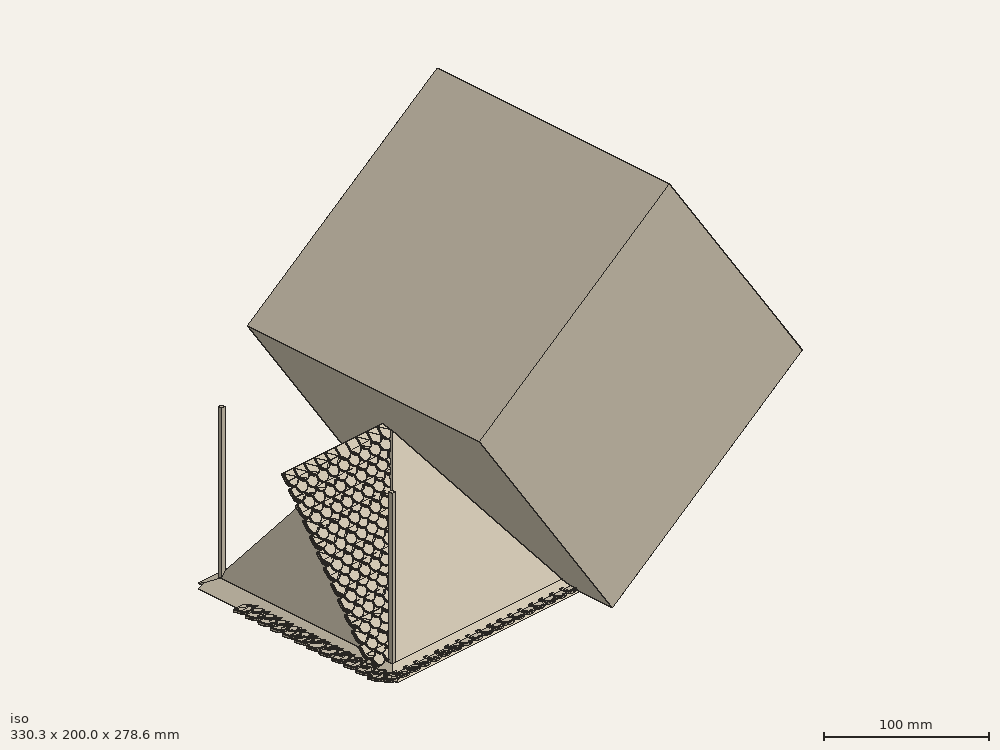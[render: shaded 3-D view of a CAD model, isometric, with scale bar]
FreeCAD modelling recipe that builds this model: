
FCSTD DOCUMENT  (FreeCAD 0.15R4671 (Git))
Label: tejado
License: All rights reserved
LicenseURL: http://en.wikipedia.org/wiki/All_rights_reserved
objects: Part::Box×20, Part::Cut×16, Part::FeaturePython×12, Sketcher::SketchObject×6, PartDesign::Pad×6, Part::Fillet×6, Part::Thickness×2, Part::MultiFuse×1
note: 75 computed .brp shape members not serialized (recipe doc carries the construction recipe); baked Part::Feature solids carry a one-line shape summary decoded from their .brp

FEATURE [Part::Box] Box  label="Cube"
  Height = 120
  Length = 144
  Width = 144
FEATURE [Part::Box] Box001  label="Cube001"
  Height = 70
  Length = 144
  Placement = pos=(0,0,0) rot=(0,-1,0;0.959931rad)
  Width = 144
FEATURE [Part::Box] Box002  label="Cube002"
  Height = 70
  Length = 144
  Placement = pos=(0,0,0) rot=(1,0,0;0.959931rad)
  Width = 144
FEATURE [Part::Box] Box003  label="Cube003"
  Height = 70
  Length = 144
  Placement = pos=(61.405,0,117.958) rot=(0,1,0;0.959931rad)
  Width = 144
FEATURE [Part::Box] Box004  label="Cube004"
  Height = 70
  Length = 144
  Placement = pos=(0,61.405,117.958) rot=(-1,0,0;0.959931rad)
  Width = 144
FEATURE [Part::Cut] Cut
  Base = -> Box
  Tool = -> Box001
FEATURE [Part::Cut] Cut001
  Base = -> Cut
  Tool = -> Box002
FEATURE [Part::Cut] Cut002
  Base = -> Cut001
  Tool = -> Box003
FEATURE [Part::Cut] Cut003  label="tejado_principal"
  Base = -> Cut002
  Tool = -> Box004
FEATURE [Part::Thickness] Thickness  label="tejado_principal_vaciado"
  Faces = -> Cut003 [Face1]
  Intersection = false
  Join = 0
  Mode = 0
  Placement = pos=(14,14,6.4) rot=(0,0,1;0rad)
  SelfIntersection = false
  Value = -2
FEATURE [Part::Box] Box005  label="Cube005"
  Height = 70
  Length = 172
  Width = 172
FEATURE [Part::Box] Box006  label="Cube006"
  Height = 70
  Length = 172
  Placement = pos=(0,0,0) rot=(1,0,0;0.436332rad)
  Width = 172
FEATURE [Part::Box] Box007  label="Cube007"
  Height = 70
  Length = 172
  Placement = pos=(0,0,0) rot=(0,-1,0;0.436332rad)
  Width = 172
FEATURE [Part::Box] Box008  label="Cube008"
  Height = 70
  Length = 172
  Placement = pos=(0,16.1151,72.6903) rot=(-1,0,0;0.436332rad)
  Width = 172
FEATURE [Part::Box] Box009  label="Cube009"
  Height = 70
  Length = 172
  Placement = pos=(16.1151,0,72.6903) rot=(0,1,0;0.436332rad)
  Width = 172
FEATURE [Part::Cut] Cut004
  Base = -> Box005
  Tool = -> Box006
FEATURE [Part::Cut] Cut005
  Base = -> Cut004
  Tool = -> Box007
FEATURE [Part::Cut] Cut006
  Base = -> Cut005
  Tool = -> Box008
FEATURE [Part::Cut] Cut007  label="faldones"
  Base = -> Cut006
  Tool = -> Box009
FEATURE [Part::Thickness] Thickness001  label="faldones_vaciado"
  Faces = -> Cut007 [Face1]
  Intersection = false
  Join = 0
  Mode = 0
  SelfIntersection = false
  Value = -2
FEATURE [Part::Box] Box010  label="Cube010"
  Height = 100
  Length = 172
  Placement = pos=(0,0,6.4) rot=(0,0,1;0rad)
  Width = 172
FEATURE [Part::Cut] Cut008  label="faldones_vaciado_completo"
  Base = -> Thickness001
  Tool = -> Box010
FEATURE [Part::Box] Box011  label="Cube011"
  Height = 10
  Length = 5
  Placement = pos=(0,0,-3) rot=(0,0,1;0rad)
  Width = 5
FEATURE [Part::Box] Box012  label="Cube012"
  Height = 10
  Length = 5
  Placement = pos=(0,167,-3) rot=(0,0,1;0rad)
  Width = 5
FEATURE [Part::Cut] Cut009
  Base = -> Cut008
  Tool = -> Box011
FEATURE [Part::Cut] Cut010  label="faldones_con_muescas"
  Base = -> Cut009
  Tool = -> Box012
FEATURE [Sketcher::SketchObject] Sketch
  Placement = pos=(9,10.5,0) rot=(0,0,1;3.14159rad)
  sketch-geometry (4):
    g0: LineSegment StartX=0 StartY=0 StartZ=0 EndX=4.1e-11 EndY=6 EndZ=0
    g1: LineSegment StartX=0 StartY=0 StartZ=0 EndX=9 EndY=0 EndZ=0
    g2: LineSegment StartX=9 StartY=0 StartZ=0 EndX=9 EndY=6 EndZ=0
    g3: ArcOfCircle CenterX=4.5 CenterY=5.99998 CenterZ=0 NormalX=0 NormalY=0 NormalZ=1 Radius=4.5 StartAngle=4.27504e-06 EndAngle=3.14159
  constraints (12):
    c: Coincident(g0,g-1)
    c: PointOnObject(g0,g-2)
    c: Coincident(g1,g-1)
    c: Horizontal(g1)
    c: Vertical(g2)
    c: Equal(g2,g0)
    c: Coincident(g3,g0)
    c: Coincident(g3,g2)
    c: DistanceX(g1) = 9
    c: Coincident(g1,g2)
    c: DistanceY(g0) = 6
    c: Radius(g3) = 4.5
FEATURE [PartDesign::Pad] Pad  label="teja"
  Length = 2
  Length2 = 100
  Placement = pos=(9,10.5,0) rot=(0,0,1;3.14159rad)
  Sketch = -> Sketch
  Type = 0
FEATURE [Part::Fillet] Fillet  label="teja_con_fillet"
  Base = -> Pad
  Edges = 4 edges r=0.5: [Edge4,Edge7,Edge10,Edge12]
FEATURE [Part::FeaturePython] Array  label="fila_tejas_par"  # Draft array (typed FeaturePython)
  Angle = 360
  ArrayType = 0
  Axis = (1,0,0)
  Base = -> Fillet
  Center = (0,0,0)
  Fuse = false
  IntervalAxis = (0,0,0)
  IntervalX = (9,0,0)
  IntervalY = (0,1,0)
  IntervalZ = (0,0,0)
  NumberPolar = 1
  NumberX = 20
  NumberY = 1
  NumberZ = 1
  Placement = pos=(0,0.102185,1.46132) rot=(-1,0,0;0.139626rad)
FEATURE [Sketcher::SketchObject] Sketch001
  Placement = pos=(9,10.5,0) rot=(0,0,1;3.14159rad)
  sketch-geometry (4):
    g0: LineSegment StartX=0 StartY=0 StartZ=0 EndX=4.1e-11 EndY=6 EndZ=0
    g1: LineSegment StartX=0 StartY=0 StartZ=0 EndX=9 EndY=0 EndZ=0
    g2: LineSegment StartX=9 StartY=0 StartZ=0 EndX=9 EndY=6 EndZ=0
    g3: ArcOfCircle CenterX=4.5 CenterY=5.99998 CenterZ=0 NormalX=0 NormalY=0 NormalZ=1 Radius=4.5 StartAngle=4.27504e-06 EndAngle=3.14159
  constraints (12):
    c: Coincident(g0,g-1)
    c: PointOnObject(g0,g-2)
    c: Coincident(g1,g-1)
    c: Horizontal(g1)
    c: Vertical(g2)
    c: Equal(g2,g0)
    c: Coincident(g3,g0)
    c: Coincident(g3,g2)
    c: DistanceX(g1) = 9
    c: Coincident(g1,g2)
    c: DistanceY(g0) = 6
    c: Radius(g3) = 4.5
FEATURE [PartDesign::Pad] Pad001  label="teja001"
  Length = 2
  Length2 = 100
  Placement = pos=(9,10.5,0) rot=(0,0,1;3.14159rad)
  Sketch = -> Sketch001
  Type = 0
FEATURE [Part::Fillet] Fillet001  label="teja_con_fillet001"
  Base = -> Pad001
  Edges = 4 edges r=0.5: [Edge4,Edge7,Edge10,Edge12]
FEATURE [Part::FeaturePython] Array001  label="fila_tejas_impar"  # Draft array (typed FeaturePython)
  Angle = 360
  ArrayType = 0
  Axis = (1,0,0)
  Base = -> Fillet001
  Center = (0,0,0)
  Fuse = false
  IntervalAxis = (0,0,0)
  IntervalX = (9,0,0)
  IntervalY = (0,1,0)
  IntervalZ = (0,0,0)
  NumberPolar = 1
  NumberX = 20
  NumberY = 1
  NumberZ = 1
  Placement = pos=(-4.5,6.10219,1.46132) rot=(-1,0,0;0.139626rad)
FEATURE [Part::FeaturePython] Array002  label="tejas"  # Draft array (typed FeaturePython)
  Angle = 360
  ArrayType = 0
  Axis = (0,0,1)
  Center = (0,0,0)
  Fuse = false
  IntervalAxis = (0,0,0)
  IntervalX = (1,0,0)
  IntervalY = (0,10.5,0)
  IntervalZ = (0,0,0)
  NumberPolar = 1
  NumberX = 1
  NumberY = 12
  NumberZ = 1
FEATURE [Sketcher::SketchObject] Sketch002
  Placement = pos=(9,10.5,0) rot=(0,0,1;3.14159rad)
  sketch-geometry (4):
    g0: LineSegment StartX=0 StartY=0 StartZ=0 EndX=4.1e-11 EndY=6 EndZ=0
    g1: LineSegment StartX=0 StartY=0 StartZ=0 EndX=9 EndY=0 EndZ=0
    g2: LineSegment StartX=9 StartY=0 StartZ=0 EndX=9 EndY=6 EndZ=0
    g3: ArcOfCircle CenterX=4.5 CenterY=5.99998 CenterZ=0 NormalX=0 NormalY=0 NormalZ=1 Radius=4.5 StartAngle=4.27504e-06 EndAngle=3.14159
  constraints (12):
    c: Coincident(g0,g-1)
    c: PointOnObject(g0,g-2)
    c: Coincident(g1,g-1)
    c: Horizontal(g1)
    c: Vertical(g2)
    c: Equal(g2,g0)
    c: Coincident(g3,g0)
    c: Coincident(g3,g2)
    c: DistanceX(g1) = 9
    c: Coincident(g1,g2)
    c: DistanceY(g0) = 6
    c: Radius(g3) = 4.5
FEATURE [PartDesign::Pad] Pad002  label="teja002"
  Length = 2
  Length2 = 100
  Placement = pos=(9,10.5,0) rot=(0,0,1;3.14159rad)
  Sketch = -> Sketch002
  Type = 0
FEATURE [Part::Fillet] Fillet002  label="teja_con_fillet002"
  Base = -> Pad002
  Edges = 4 edges r=0.5: [Edge4,Edge7,Edge10,Edge12]
FEATURE [Part::FeaturePython] Array003  label="fila_tejas_003"  # Draft array (typed FeaturePython)
  Angle = 360
  ArrayType = 0
  Axis = (1,0,0)
  Base = -> Fillet002
  Center = (0,0,0)
  Fuse = false
  IntervalAxis = (0,0,0)
  IntervalX = (9,0,0)
  IntervalY = (0,1,0)
  IntervalZ = (0,0,0)
  NumberPolar = 1
  NumberX = 20
  NumberY = 1
  NumberZ = 1
  Placement = pos=(0,0.102185,1.46132) rot=(-1,0,0;0.139626rad)
FEATURE [Sketcher::SketchObject] Sketch003
  Placement = pos=(9,10.5,0) rot=(0,0,1;3.14159rad)
  sketch-geometry (4):
    g0: LineSegment StartX=0 StartY=0 StartZ=0 EndX=4.1e-11 EndY=6 EndZ=0
    g1: LineSegment StartX=0 StartY=0 StartZ=0 EndX=9 EndY=0 EndZ=0
    g2: LineSegment StartX=9 StartY=0 StartZ=0 EndX=9 EndY=6 EndZ=0
    g3: ArcOfCircle CenterX=4.5 CenterY=5.99998 CenterZ=0 NormalX=0 NormalY=0 NormalZ=1 Radius=4.5 StartAngle=4.27504e-06 EndAngle=3.14159
  constraints (12):
    c: Coincident(g0,g-1)
    c: PointOnObject(g0,g-2)
    c: Coincident(g1,g-1)
    c: Horizontal(g1)
    c: Vertical(g2)
    c: Equal(g2,g0)
    c: Coincident(g3,g0)
    c: Coincident(g3,g2)
    c: DistanceX(g1) = 9
    c: Coincident(g1,g2)
    c: DistanceY(g0) = 6
    c: Radius(g3) = 4.5
FEATURE [PartDesign::Pad] Pad003  label="teja003"
  Length = 2
  Length2 = 100
  Placement = pos=(9,10.5,0) rot=(0,0,1;3.14159rad)
  Sketch = -> Sketch003
  Type = 0
FEATURE [Part::Fillet] Fillet003  label="teja_con_fillet003"
  Base = -> Pad003
  Edges = 4 edges r=0.5: [Edge4,Edge7,Edge10,Edge12]
FEATURE [Part::FeaturePython] Array004  label="fila_tejas_004"  # Draft array (typed FeaturePython)
  Angle = 360
  ArrayType = 0
  Axis = (1,0,0)
  Base = -> Fillet003
  Center = (0,0,0)
  Fuse = false
  IntervalAxis = (0,0,0)
  IntervalX = (9,0,0)
  IntervalY = (0,1,0)
  IntervalZ = (0,0,0)
  NumberPolar = 1
  NumberX = 20
  NumberY = 1
  NumberZ = 1
  Placement = pos=(-4.5,6.10219,1.46132) rot=(-1,0,0;0.139626rad)
FEATURE [Part::MultiFuse] Fusion001  label="fila_doble_tejas001"
  Shapes = -> [Array003,Array004]
FEATURE [Part::FeaturePython] Array005  label="tejas_norte"  # Draft array (typed FeaturePython)
  Angle = 360
  ArrayType = 0
  Axis = (0,0,1)
  Base = -> Fusion001
  Center = (0,0,0)
  Fuse = false
  IntervalAxis = (0,0,0)
  IntervalX = (1,0,0)
  IntervalY = (0,10.5,0)
  IntervalZ = (0,0,0)
  NumberPolar = 1
  NumberX = 1
  NumberY = 12
  NumberZ = 1
  Placement = pos=(0,15.5,5.5) rot=(1,0,0;0.959931rad)
FEATURE [Part::Box] Box015  label="Cube015"
  Height = 120
  Length = 150
  Placement = pos=(-3,-3,0) rot=(0,0,1;0rad)
  Width = 150
FEATURE [Part::Box] Box016  label="Cube016"
  Height = 70
  Length = 144
  Placement = pos=(-3,0,0) rot=(0,-1,0;0.959931rad)
  Width = 144
FEATURE [Part::Box] Box017  label="Cube017"
  Height = 70
  Length = 144
  Placement = pos=(0,-3,0) rot=(1,0,0;0.959931rad)
  Width = 144
FEATURE [Part::Box] Box018  label="Cube018"
  Height = 70
  Length = 144
  Placement = pos=(64.405,0,117.958) rot=(0,1,0;0.959931rad)
  Width = 144
FEATURE [Part::Box] Box019  label="Cube019"
  Height = 70
  Length = 144
  Placement = pos=(0,64.405,117.958) rot=(-1,0,0;0.959931rad)
  Width = 144
FEATURE [Part::Cut] Cut011
  Base = -> Box015
  Tool = -> Box016
FEATURE [Part::Cut] Cut012
  Base = -> Cut011
  Tool = -> Box017
FEATURE [Part::Cut] Cut013
  Base = -> Cut012
  Tool = -> Box018
FEATURE [Part::Cut] Cut014  label="tejado_principal001"
  Base = -> Cut013
  Placement = pos=(14,14,6.4) rot=(0,0,1;0rad)
  Tool = -> Box019
FEATURE [Part::FeaturePython] Array006  label="filas_tejas_par"  # Draft array (typed FeaturePython)
  Angle = 360
  ArrayType = 0
  Axis = (0,0,1)
  Base = -> Array
  Center = (0,0,0)
  Fuse = false
  IntervalAxis = (0,0,0)
  IntervalX = (1,0,0)
  IntervalY = (0,10.5,0)
  IntervalZ = (0,0,0)
  NumberPolar = 1
  NumberX = 1
  NumberY = 12
  NumberZ = 1
  Placement = pos=(0,15.5,5.5) rot=(1,0,0;0.959931rad)
FEATURE [Part::FeaturePython] Array007  label="filas_tejas_impar"  # Draft array (typed FeaturePython)
  Angle = 360
  ArrayType = 0
  Axis = (0,0,1)
  Base = -> Array001
  Center = (0,0,0)
  Fuse = false
  IntervalAxis = (0,0,0)
  IntervalX = (1,0,0)
  IntervalY = (0,10.5,0)
  IntervalZ = (0,0,0)
  NumberPolar = 1
  NumberX = 1
  NumberY = 12
  NumberZ = 1
  Placement = pos=(0,15.5,5.5) rot=(1,0,0;0.959931rad)
FEATURE [Sketcher::SketchObject] Sketch004
  Placement = pos=(9,10.5,0) rot=(0,0,1;3.14159rad)
  sketch-geometry (4):
    g0: LineSegment StartX=0 StartY=0 StartZ=0 EndX=4.1e-11 EndY=6 EndZ=0
    g1: LineSegment StartX=0 StartY=0 StartZ=0 EndX=9 EndY=0 EndZ=0
    g2: LineSegment StartX=9 StartY=0 StartZ=0 EndX=9 EndY=6 EndZ=0
    g3: ArcOfCircle CenterX=4.5 CenterY=5.99998 CenterZ=0 NormalX=0 NormalY=0 NormalZ=1 Radius=4.5 StartAngle=4.27504e-06 EndAngle=3.14159
  constraints (12):
    c: Coincident(g0,g-1)
    c: PointOnObject(g0,g-2)
    c: Coincident(g1,g-1)
    c: Horizontal(g1)
    c: Vertical(g2)
    c: Equal(g2,g0)
    c: Coincident(g3,g0)
    c: Coincident(g3,g2)
    c: DistanceX(g1) = 9
    c: Coincident(g1,g2)
    c: DistanceY(g0) = 6
    c: Radius(g3) = 4.5
FEATURE [PartDesign::Pad] Pad004  label="teja004"
  Length = 2
  Length2 = 100
  Placement = pos=(9,10.5,0) rot=(0,0,1;3.14159rad)
  Sketch = -> Sketch004
  Type = 0
FEATURE [Part::Fillet] Fillet004  label="teja_con_fillet004"
  Base = -> Pad004
  Edges = 4 edges r=0.5: [Edge4,Edge7,Edge10,Edge12]
FEATURE [Part::FeaturePython] Array008  label="fila_tejas_par001"  # Draft array (typed FeaturePython)
  Angle = 360
  ArrayType = 0
  Axis = (1,0,0)
  Base = -> Fillet004
  Center = (0,0,0)
  Fuse = false
  IntervalAxis = (0,0,0)
  IntervalX = (9,0,0)
  IntervalY = (0,1,0)
  IntervalZ = (0,0,0)
  NumberPolar = 1
  NumberX = 20
  NumberY = 1
  NumberZ = 1
  Placement = pos=(0,0.102185,1.46132) rot=(-1,0,0;0.139626rad)
FEATURE [Sketcher::SketchObject] Sketch005
  Placement = pos=(9,10.5,0) rot=(0,0,1;3.14159rad)
  sketch-geometry (4):
    g0: LineSegment StartX=0 StartY=0 StartZ=0 EndX=4.1e-11 EndY=6 EndZ=0
    g1: LineSegment StartX=0 StartY=0 StartZ=0 EndX=9 EndY=0 EndZ=0
    g2: LineSegment StartX=9 StartY=0 StartZ=0 EndX=9 EndY=6 EndZ=0
    g3: ArcOfCircle CenterX=4.5 CenterY=5.99998 CenterZ=0 NormalX=0 NormalY=0 NormalZ=1 Radius=4.5 StartAngle=4.27504e-06 EndAngle=3.14159
  constraints (12):
    c: Coincident(g0,g-1)
    c: PointOnObject(g0,g-2)
    c: Coincident(g1,g-1)
    c: Horizontal(g1)
    c: Vertical(g2)
    c: Equal(g2,g0)
    c: Coincident(g3,g0)
    c: Coincident(g3,g2)
    c: DistanceX(g1) = 9
    c: Coincident(g1,g2)
    c: DistanceY(g0) = 6
    c: Radius(g3) = 4.5
FEATURE [PartDesign::Pad] Pad005  label="teja005"
  Length = 2
  Length2 = 100
  Placement = pos=(9,10.5,0) rot=(0,0,1;3.14159rad)
  Sketch = -> Sketch005
  Type = 0
FEATURE [Part::Fillet] Fillet005  label="teja_con_fillet005"
  Base = -> Pad005
  Edges = 4 edges r=0.5: [Edge4,Edge7,Edge10,Edge12]
FEATURE [Part::FeaturePython] Array009  label="fila_tejas_impar001"  # Draft array (typed FeaturePython)
  Angle = 360
  ArrayType = 0
  Axis = (1,0,0)
  Base = -> Fillet005
  Center = (0,0,0)
  Fuse = false
  IntervalAxis = (0,0,0)
  IntervalX = (9,0,0)
  IntervalY = (0,1,0)
  IntervalZ = (0,0,0)
  NumberPolar = 1
  NumberX = 20
  NumberY = 1
  NumberZ = 1
  Placement = pos=(-4.5,6.10219,1.46132) rot=(-1,0,0;0.139626rad)
FEATURE [Part::FeaturePython] Array010  label="filas_tejas_par001"  # Draft array (typed FeaturePython)
  Angle = 360
  ArrayType = 0
  Axis = (0,0,1)
  Base = -> Array008
  Center = (0,0,0)
  Fuse = false
  IntervalAxis = (0,0,0)
  IntervalX = (1,0,0)
  IntervalY = (0,10.5,0)
  IntervalZ = (0,0,0)
  NumberPolar = 1
  NumberX = 1
  NumberY = 12
  NumberZ = 1
FEATURE [Part::FeaturePython] Array011  label="filas_tejas_impar001"  # Draft array (typed FeaturePython)
  Angle = 360
  ArrayType = 0
  Axis = (0,0,1)
  Base = -> Array009
  Center = (0,0,0)
  Fuse = false
  IntervalAxis = (0,0,0)
  IntervalX = (1,0,0)
  IntervalY = (0,10.5,0)
  IntervalZ = (0,0,0)
  NumberPolar = 1
  NumberX = 1
  NumberY = 12
  NumberZ = 1
FEATURE [Part::Box] Box020  label="Cube020"
  Height = 200
  Length = 200
  Placement = pos=(10,0,0) rot=(0,-1,0;0.959931rad)
  Width = 200
FEATURE [Part::Box] Box021  label="Cube021"
  Height = 200
  Length = 200
  Placement = pos=(162,172,0) rot=(0.461749,0,0.887011;3.14159rad)
  Width = 200
FEATURE [Part::Cut] Cut015
  Base = -> Array006
  Tool = -> Box020
